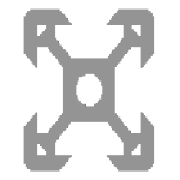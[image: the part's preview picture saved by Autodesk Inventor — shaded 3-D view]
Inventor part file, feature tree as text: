
AUTODESK INVENTOR PART (.ipt)
format: ipt  version: 2017.3 (Build 213256000, 256)  size: 196,096 bytes
history: native  units: mm
features: other x3, sketch x3, plane x1
ambient origin geometry x8: Origin, YZ Plane, XZ Plane, XY Plane, X Axis, Y Axis, Z Axis, Center Point
bodies: Solid1 (feature_tree), Body (feature_tree)
feature tree (7):
  other  "Driven Length"
  other  "Start Plane"
  other  "End Plane"
  sketch  "Sketch1"  dims[d2=4.2mm]
  sketch  "Sketch4"  dims[d3=1.5mm]
  plane  "Work Plane4"
  sketch  "Sketch5"  dims[d4=1.64mm d5=1.8mm d6=5.68mm d7=1.8mm d9=1.5mm d12=-0.0mm d13=470.0mm d14=0.13mm d15=0.0mm d18=90.0deg d17=470.0mm]
